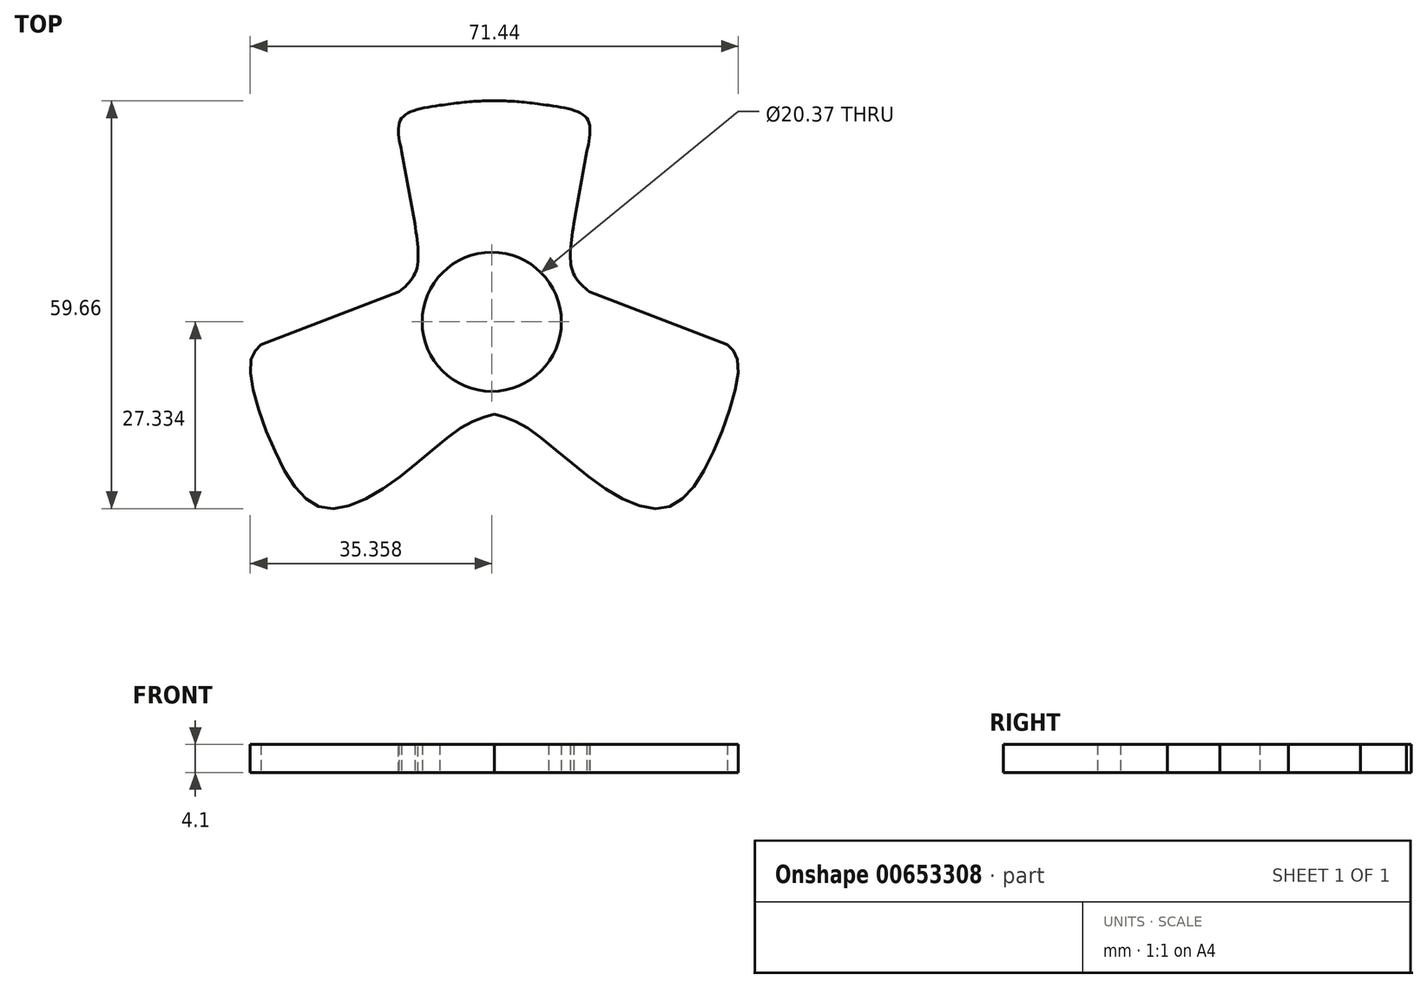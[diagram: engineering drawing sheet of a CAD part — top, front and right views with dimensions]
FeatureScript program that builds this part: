
annotation { "Feature Type Name" : "Feature", "Feature Type Description" : "" }
export const myFeature = defineFeature(function(context is Context, id is Id, definition is map)
    precondition{}
    {
        {
            var Q0;
            Q0=qCreatedBy(makeId("Top.planeOp"),FACE);
            var sketch = newSketch(context, id + "F0", { "sketchPlane" : qUnion([Q0])});
            skLineSegment(sketch, "E0", {"start": v(-34.13, -2.5) * mm, "end": v(-13.94, 5.2) * mm});
            skFitSpline(sketch, "E1", {"points": [v(-13.94, 5.2) * mm, v(-11.44, 8.27) * mm, v(-11.63, 15.2) * mm], "startDerivative": vector(7.13, 6.06) * mm, "endDerivative": vector(-2.09, 13.59) * mm});
            skLineSegment(sketch, "E2", {"start": v(-11.63, 15.2) * mm, "end": v(-13.56, 25.77) * mm});
            skFitSpline(sketch, "E3", {"points": [v(-13.56, 25.77) * mm, v(-13.56, 30.58) * mm, v(-7.98, 32.5) * mm], "startDerivative": vector(-2.52, 11.67) * mm, "endDerivative": vector(13.4, 1.96) * mm});
            skFitSpline(sketch, "E4", {"points": [v(-7.98, 32.5) * mm, v(-2.94, 33.08) * mm, v(0, 33.15) * mm], "startDerivative": vector(9.47, 1.27) * mm, "endDerivative": vector(6.35, -0.03) * mm});
            skFitSpline(sketch, "E5", {"points": [v(-34.13, -2.5) * mm, v(-35.68, -5.11) * mm, v(-32.12, -18.05) * mm, v(-25.33, -26.3) * mm, v(-15.46, -23.06) * mm, v(-4.79, -14.65) * mm, v(0, -12.71) * mm], "startDerivative": vector(-20.94, -20.16) * mm, "endDerivative": vector(35.09, 9.43) * mm});
            skFitSpline(sketch, "E6.MirrorCS", {"points": [v(13.56, 25.77) * mm, v(13.56, 30.58) * mm, v(7.98, 32.5) * mm], "startDerivative": vector(2.52, 11.67) * mm, "endDerivative": vector(-13.4, 1.96) * mm});
            skFitSpline(sketch, "E7.MirrorCS", {"points": [v(13.94, 5.2) * mm, v(11.44, 8.27) * mm, v(11.63, 15.2) * mm], "startDerivative": vector(-7.13, 6.06) * mm, "endDerivative": vector(2.09, 13.59) * mm});
            skFitSpline(sketch, "E8.MirrorCS", {"points": [v(7.98, 32.5) * mm, v(2.94, 33.08) * mm, v(0, 33.15) * mm], "startDerivative": vector(-9.47, 1.27) * mm, "endDerivative": vector(-6.35, -0.03) * mm});
            skLineSegment(sketch, "E9.MirrorCS", {"start": v(11.63, 15.2) * mm, "end": v(13.56, 25.77) * mm});
            skLineSegment(sketch, "E10.MirrorCS", {"start": v(34.13, -2.5) * mm, "end": v(13.94, 5.2) * mm});
            skFitSpline(sketch, "E11.MirrorCS", {"points": [v(34.13, -2.5) * mm, v(35.68, -5.11) * mm, v(32.12, -18.05) * mm, v(25.33, -26.3) * mm, v(15.46, -23.06) * mm, v(4.79, -14.65) * mm, v(0, -12.71) * mm], "startDerivative": vector(20.94, -20.16) * mm, "endDerivative": vector(-35.09, 9.43) * mm});
            skSolve(sketch);
        }
        {
            var Q0;
            Q0=makeQuery(id+"F0.imprint","IMPRINT",FACE,{"disambiguationData":[TD([[makeQuery(id+"F0.imprint","IMPRINT",EDGE,{"derivedFrom":sQuery(id+"F0.wireOp",EDGE,"E0")}),-1.0]])]});
            var sketch = newSketch(context, id + "F1", { "sketchPlane" : qUnion([Q0])});
            skCircle(sketch, "E12", {"center": v(-0.36, 0.82) * mm, "radius": 10.18 * mm});
            skSolve(sketch);
        }
        {
            var Q0;
            Q0=makeQuery(id+"F0.imprint","IMPRINT",FACE,{"disambiguationData":[TD([[makeQuery(id+"F0.imprint","IMPRINT",EDGE,{"derivedFrom":sQuery(id+"F0.wireOp",EDGE,"E0")}),-1.0]])]});
            extrude(context, id + "F2", {"entities" : qUnion([Q0]), "depth" : 4.1 * mm, "offsetDistance" : 25 * mm});
        }
        {
            var Q0;
            Q0 = qSketchRegion(id + "F1", true);
            extrude(context, id + "F3", {"entities" : qUnion([Q0]), "operationType" : NewBodyOperationType.REMOVE, "depth" : 4.6 * mm, "offsetDistance" : 25 * mm});
        }
    });
